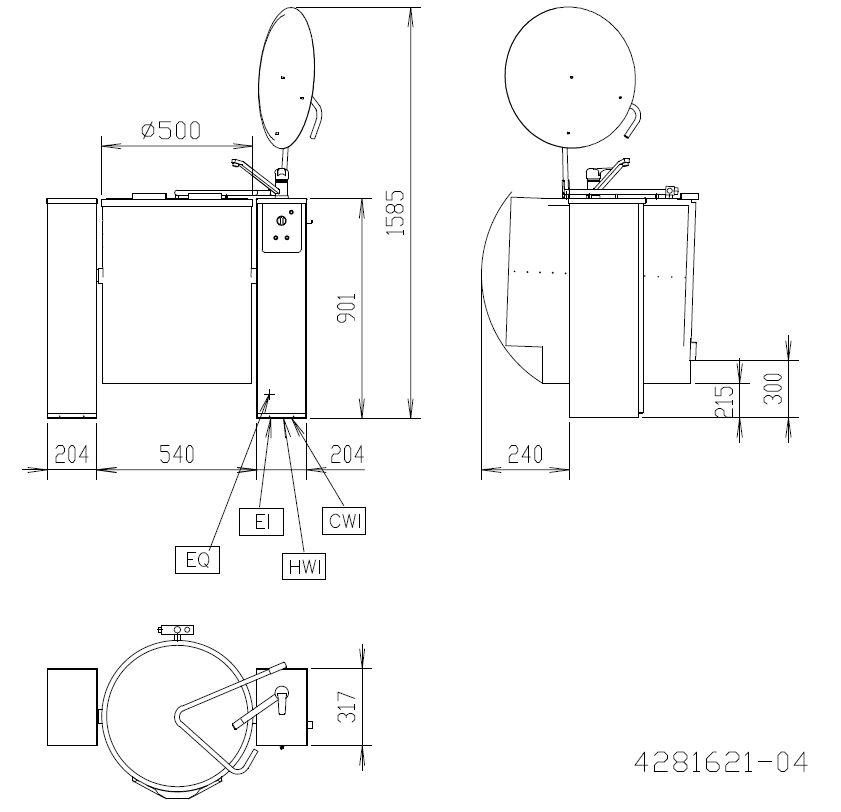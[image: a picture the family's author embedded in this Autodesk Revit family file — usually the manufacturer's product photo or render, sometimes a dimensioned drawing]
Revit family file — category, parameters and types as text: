
# Revit family: QF_ZANUSSI_232165_PE040
name_source: partatom
category: Attrezzature speciali
units: mm (PartAtom-declared; Revit-internal decimal feet)

## family parameters
Basato su piano di lavoro = No
Condiviso = No
Punto di calcolo locali = No
Quota connettore circolare = Usa diametro
Sempre verticale = Sì
Taglio con vuoti quando caricato = No
Tipo di parte = Normale

## types (1)
- Standard
    Accessory = Sì
    Cold Water Size = 13 mm
    Compressed Air Pressure = 0.0 Pa
    Compressed Air Size = 0 mm
    Compressed Air Volume = 0.0 L/s
    Condensate Return Size = 0 mm
    Cycle = 50 Hz
    Depth Actual = 660 mm
    Descrizione = ELECTRIC TILTING BOILING PAN 40L
    Direct Waste Size = 0 mm
    Gas Input Pressure = 0
    Gas KW = 0
    Gas Size = 0 mm
    HP = 16.1 HP
    Height Actual = 900 mm  [stored 2.95276 ft]
    Hot Water Size = 13 mm
    Item Number = 232165
    Length Actual = 948 mm  [stored 3.11024 ft]
    Modello = PE040
    Phase = 3
    Produttore = Zanussi
    Prospetto di default = 0 mm  [stored 0 ft]
    Refrigerant Compressor Remote = Sì
    Refrigeration Liquid Line Size = 0 mm  [stored 0 ft]
    Refrigeration Suction Line Size = 0 mm  [stored 0 ft]
    Steam Consumption per Hour = 0
    Steam Supply Maximum Pressure = 0.0 Pa
    Steam Supply Minimum Pressure = 0.0 Pa
    Steam Supply Size = 0 mm
    URL = http://www.zanussiprofessional.com
    URL Manufacturer = http://www.zanussiprofessional.com
    Volts = 400 V
    Watts = 12000 W
    Weight = 87.00 kg

note: source unit labels omitted for Gas Input Pressure — the stored unit's dimension contradicts the parameter name (converter mislabeling)

note: [stored X ft] marks values corroborated as IEEE doubles in the binary element streams (Revit-internal decimal feet)

## geometry (parser evidence)
native form markers: Sweep x9
no freeform markers — native parametric forms only
